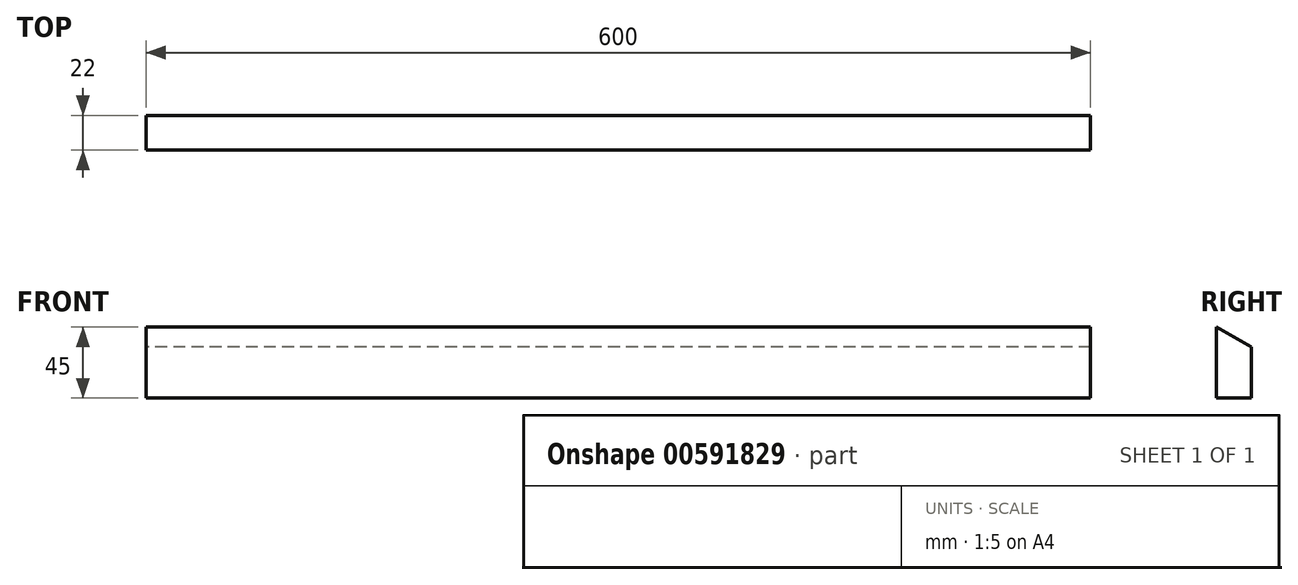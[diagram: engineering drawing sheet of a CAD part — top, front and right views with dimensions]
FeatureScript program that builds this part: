
annotation { "Feature Type Name" : "Feature", "Feature Type Description" : "" }
export const myFeature = defineFeature(function(context is Context, id is Id, definition is map)
    precondition{}
    {
        {
            var Q0;
            Q0=qCreatedBy(makeId("Right.planeOp"),FACE);
            var sketch = newSketch(context, id + "F0", { "sketchPlane" : qUnion([Q0])});
            skLineSegment(sketch, "E0", {"start": v(0, 0) * mm, "end": v(22, 0) * mm});
            skLineSegment(sketch, "E1", {"start": v(22, 0) * mm, "end": v(22, 32.3) * mm});
            skLineSegment(sketch, "E2", {"start": v(22, 32.3) * mm, "end": v(0, 45) * mm});
            skLineSegment(sketch, "E3", {"start": v(0, 45) * mm, "end": v(0, 0) * mm});
            skSolve(sketch);
        }
        {
            var Q0;
            Q0=makeQuery(id+"F0.imprint","IMPRINT",FACE,{"disambiguationData":[TD([[makeQuery(id+"F0.imprint","IMPRINT",EDGE,{"derivedFrom":sQuery(id+"F0.wireOp",EDGE,"E0")}),1.0]])]});
            extrude(context, id + "F1", {"entities" : qUnion([Q0]), "depth" : 600 * mm, "offsetDistance" : 25 * mm});
        }
    });
